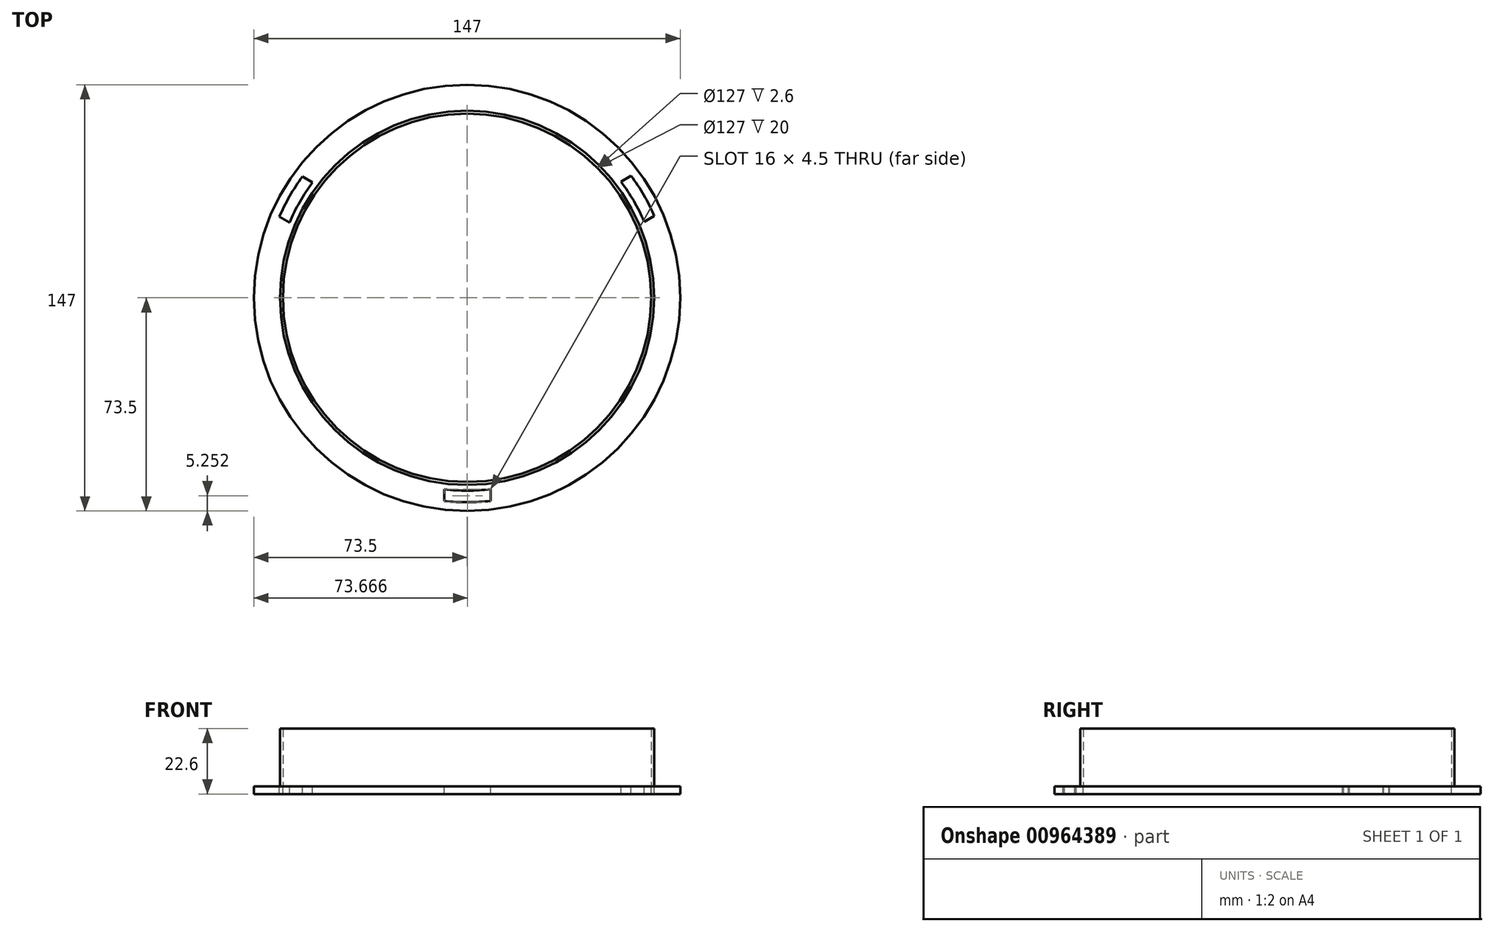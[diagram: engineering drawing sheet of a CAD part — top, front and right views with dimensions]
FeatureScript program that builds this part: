
annotation { "Feature Type Name" : "Feature", "Feature Type Description" : "" }
export const myFeature = defineFeature(function(context is Context, id is Id, definition is map)
    precondition{}
    {
        {
            var Q0;
            Q0=qCreatedBy(makeId("Top.planeOp"),FACE);
            var sketch = newSketch(context, id + "F0", { "sketchPlane" : qUnion([Q0])});
            skCircle(sketch, "E0", {"center": v(0, 0) * mm, "radius": 63.5 * mm});
            skCircle(sketch, "E1", {"center": v(0, 0) * mm, "radius": 64.5 * mm});
            skSolve(sketch);
        }
        {
            var Q0;
            Q0=makeQuery(id+"F0.imprint","IMPRINT",FACE,{"disambiguationData":[TD([[makeQuery(id+"F0.imprint","IMPRINT",EDGE,{"derivedFrom":sQuery(id+"F0.wireOp",EDGE,"E0")}),-1.0]])]});
            extrude(context, id + "F1", {"entities" : qUnion([Q0]), "depth" : 20 * mm, "offsetDistance" : 25 * mm});
        }
        {
            var Q0;
            Q0=makeQuery(id+"F1.opExtrude","CAP_FACE",FACE,{"disambiguationData":[OSD([sQuery(id+"F0.wireOp",EDGE,"E0"),sQuery(id+"F0.wireOp",EDGE,"E1")])],"isStart":true});
            var sketch = newSketch(context, id + "F2", { "sketchPlane" : qUnion([Q0])});
            skCircle(sketch, "E2", {"center": v(0, 0) * mm, "radius": 73.5 * mm});
            skLineSegment(sketch, "E3", {"start": v(-7.83, 70.06) * mm, "end": v(-7.83, 66.04) * mm});
            skLineSegment(sketch, "E4", {"start": v(8.17, 70.03) * mm, "end": v(8.17, 66) * mm});
            skArc(sketch, "E5", {"start": v(-7.83, 70.06) * mm, "mid": v(0.17, 70.5) * mm, "end": v(8.17, 70.03) * mm});
            skArc(sketch, "E6", {"start": v(-7.83, 66.04) * mm, "mid": v(0.17, 66.5) * mm, "end": v(8.17, 66) * mm});
            skLineSegment(sketch, "E7.1.0", {"start": v(-56.76, -41.82) * mm, "end": v(-53.27, -39.8) * mm});
            skArc(sketch, "E7.1.1", {"start": v(-56.76, -41.82) * mm, "mid": v(-61.14, -35.1) * mm, "end": v(-64.73, -27.94) * mm});
            skLineSegment(sketch, "E7.1.2", {"start": v(-64.73, -27.94) * mm, "end": v(-61.24, -25.93) * mm});
            skArc(sketch, "E7.1.3", {"start": v(-53.27, -39.8) * mm, "mid": v(-57.67, -33.1) * mm, "end": v(-61.24, -25.93) * mm});
            skLineSegment(sketch, "E7.2.0", {"start": v(64.6, -28.25) * mm, "end": v(61.1, -26.23) * mm});
            skArc(sketch, "E7.2.1", {"start": v(64.6, -28.25) * mm, "mid": v(60.97, -35.4) * mm, "end": v(56.56, -42.08) * mm});
            skLineSegment(sketch, "E7.2.2", {"start": v(56.56, -42.08) * mm, "end": v(53.07, -40.07) * mm});
            skArc(sketch, "E7.2.3", {"start": v(61.1, -26.23) * mm, "mid": v(57.5, -33.4) * mm, "end": v(53.07, -40.07) * mm});
            skCircle(sketch, "E8", {"center": v(0, 0) * mm, "radius": 63.5 * mm});
            skSolve(sketch);
        }
        {
            var Q0;
            Q0=makeQuery(id+"F2.imprint","IMPRINT",FACE,{"disambiguationData":[TD([[makeQuery(id+"F2.imprint","IMPRINT",EDGE,{"derivedFrom":sQuery(id+"F2.wireOp",EDGE,"E2")}),1.0]])]});
            var Q1;
            Q1=makeQuery(id+"F2.imprint","IMPRINT",FACE,{"disambiguationData":[TD([[makeQuery(id+"F2.imprint","IMPRINT",EDGE,{"derivedFrom":sQuery(id+"F2.wireOp",EDGE,"E8")}),1.0]])]});
            extrude(context, id + "F3", {"entities" : qUnion([Q0, Q1]), "depth" : 2.6 * mm, "offsetDistance" : 25 * mm});
        }
    });
